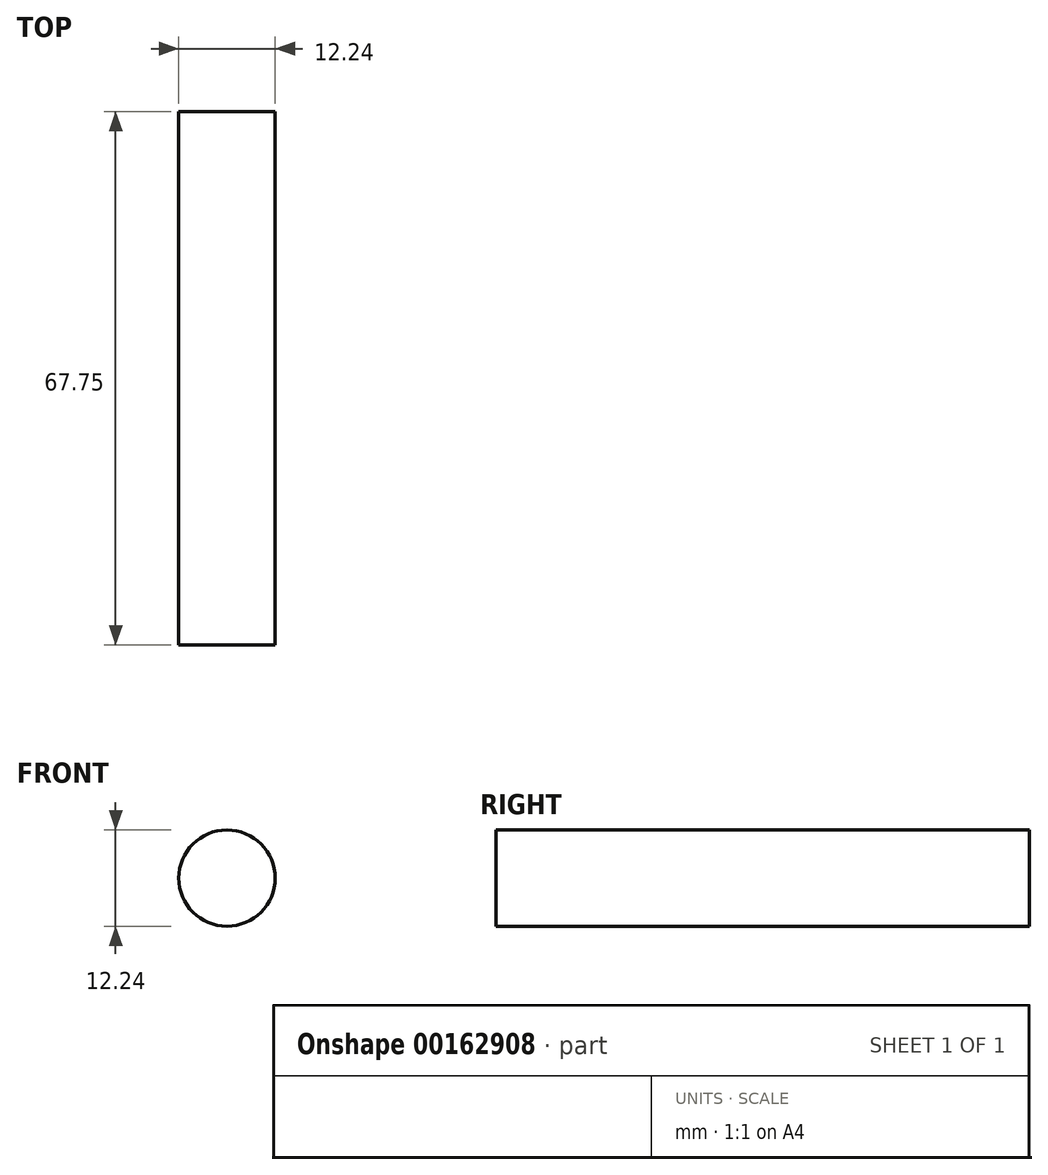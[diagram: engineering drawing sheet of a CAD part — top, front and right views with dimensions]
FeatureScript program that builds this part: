
annotation { "Feature Type Name" : "Feature", "Feature Type Description" : "" }
export const myFeature = defineFeature(function(context is Context, id is Id, definition is map)
    precondition{}
    {
        {
            var Q0;
            Q0=qCreatedBy(makeId("Front.planeOp"),FACE);
            var sketch = newSketch(context, id + "F0", { "sketchPlane" : qUnion([Q0])});
            skCircle(sketch, "E0", {"center": v(0, 0) * mm, "radius": 6.12 * mm});
            skSolve(sketch);
        }
        {
            var Q0;
            Q0 = qSketchRegion(id + "F0", true);
            extrude(context, id + "F1", {"entities" : qUnion([Q0]), "depth" : 67.75 * mm});
        }
    });
